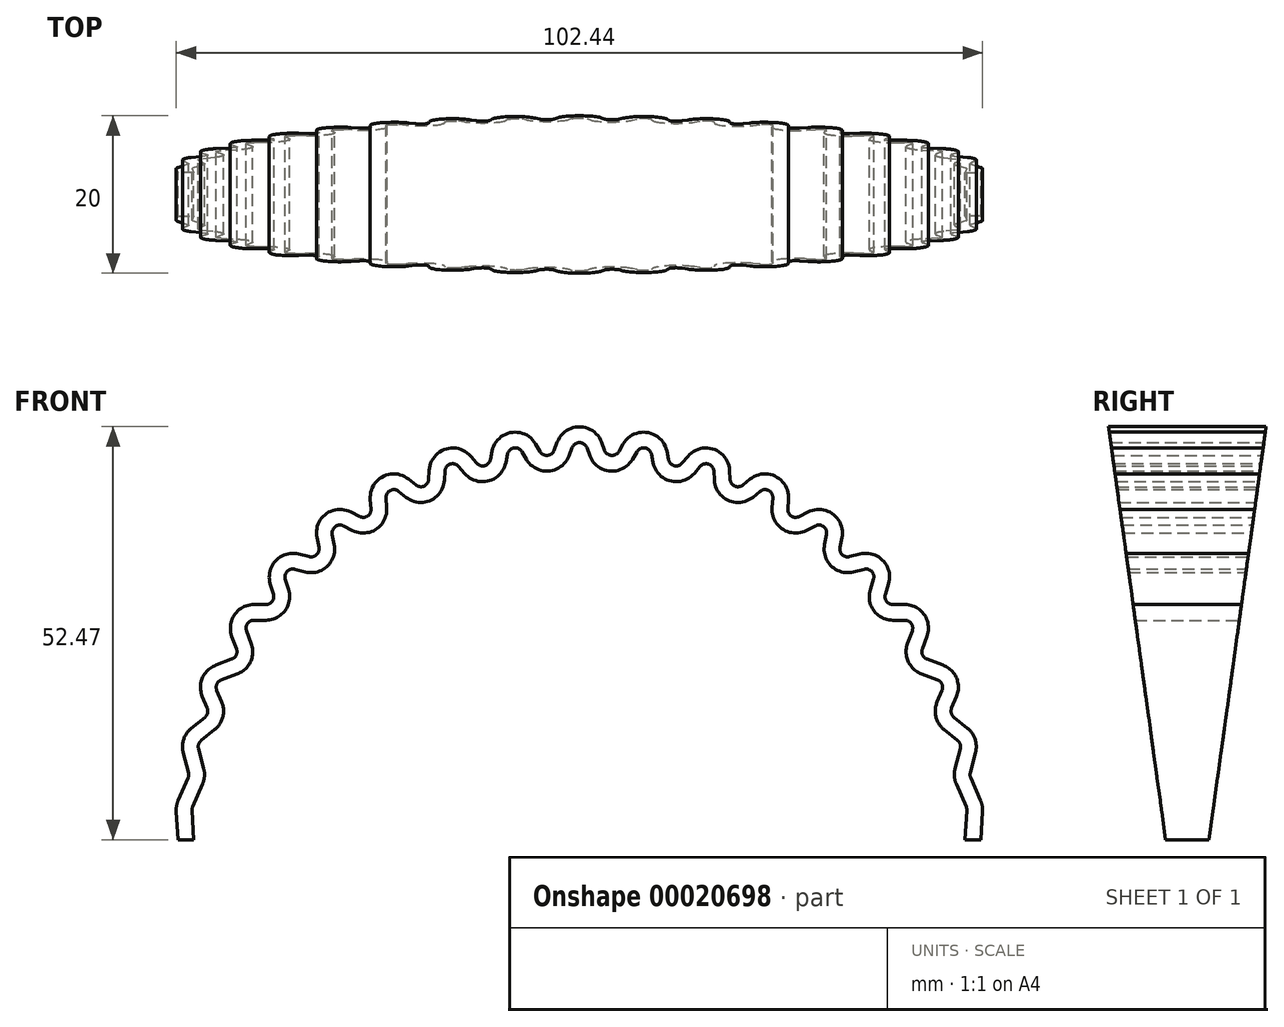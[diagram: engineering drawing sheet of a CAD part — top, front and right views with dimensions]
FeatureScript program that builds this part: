
annotation { "Feature Type Name" : "Feature", "Feature Type Description" : "" }
export const myFeature = defineFeature(function(context is Context, id is Id, definition is map)
    precondition{}
    {
        {
            var Q0;
            Q0=qCreatedBy(makeId("Front.planeOp"),FACE);
            var sketch = newSketch(context, id + "F0", { "sketchPlane" : qUnion([Q0])});
            skCircle(sketch, "E0", {"center": v(0, 0) * mm, "radius": 50 * mm});
            skCircle(sketch, "E1", {"center": v(0, 5) * mm, "radius": 50.25 * mm});
            skCircle(sketch, "E2", {"center": v(0, -5) * mm, "radius": 50.25 * mm});
            skLineSegment(sketch, "E3", {"start": v(0, 0) * mm, "end": v(-50, 0) * mm, "construction": true});
            skLineSegment(sketch, "E4.1.0", {"start": v(0, 0) * mm, "end": v(-49.83, 4.13) * mm, "construction": true});
            skLineSegment(sketch, "E4.2.0", {"start": v(0, 0) * mm, "end": v(-49.32, 8.23) * mm, "construction": true});
            skLineSegment(sketch, "E4.3.0", {"start": v(0, 0) * mm, "end": v(-48.47, 12.27) * mm, "construction": true});
            skLineSegment(sketch, "E4.4.0", {"start": v(0, 0) * mm, "end": v(-47.3, 16.23) * mm, "construction": true});
            skLineSegment(sketch, "E4.5.0", {"start": v(0, 0) * mm, "end": v(-45.79, 20.08) * mm, "construction": true});
            skLineSegment(sketch, "E4.6.0", {"start": v(0, 0) * mm, "end": v(-43.97, 23.8) * mm, "construction": true});
            skLineSegment(sketch, "E4.7.0", {"start": v(0, 0) * mm, "end": v(-41.86, 27.35) * mm, "construction": true});
            skLineSegment(sketch, "E4.anchor2", {"start": v(0, 0) * mm, "end": v(0, 50) * mm, "construction": true});
            skLineSegment(sketch, "E5.2.8.0", {"start": v(0, 0) * mm, "end": v(-39.46, 30.71) * mm, "construction": true});
            skLineSegment(sketch, "E5.2.9.0", {"start": v(0, 0) * mm, "end": v(-36.79, 33.86) * mm, "construction": true});
            skLineSegment(sketch, "E5.2.10.0", {"start": v(0, 0) * mm, "end": v(-33.86, 36.79) * mm, "construction": true});
            skLineSegment(sketch, "E5.2.11.0", {"start": v(0, 0) * mm, "end": v(-30.71, 39.46) * mm, "construction": true});
            skLineSegment(sketch, "E5.2.12.0", {"start": v(0, 0) * mm, "end": v(-27.35, 41.86) * mm, "construction": true});
            skLineSegment(sketch, "E6.2.13.0", {"start": v(0, 0) * mm, "end": v(-23.8, 43.97) * mm, "construction": true});
            skLineSegment(sketch, "E6.2.14.0", {"start": v(0, 0) * mm, "end": v(-20.08, 45.79) * mm, "construction": true});
            skLineSegment(sketch, "E6.2.15.0", {"start": v(0, 0) * mm, "end": v(-16.23, 47.3) * mm, "construction": true});
            skLineSegment(sketch, "E6.2.16.0", {"start": v(0, 0) * mm, "end": v(-12.27, 48.47) * mm, "construction": true});
            skLineSegment(sketch, "E6.2.17.0", {"start": v(0, 0) * mm, "end": v(-8.23, 49.32) * mm, "construction": true});
            skLineSegment(sketch, "E6.2.18.0", {"start": v(0, 0) * mm, "end": v(-4.13, 49.83) * mm, "construction": true});
            skLineSegment(sketch, "E7", {"start": v(-50, 0) * mm, "end": v(-50.24, 4.13) * mm});
            skLineSegment(sketch, "E8", {"start": v(-50.24, 4.13) * mm, "end": v(-48.51, 8.1) * mm});
            skLineSegment(sketch, "E9", {"start": v(-48.51, 8.1) * mm, "end": v(-49.67, 12.58) * mm});
            skLineSegment(sketch, "E10", {"start": v(-49.67, 12.58) * mm, "end": v(-45.78, 15.72) * mm});
            skLineSegment(sketch, "E11", {"start": v(-45.78, 15.72) * mm, "end": v(-47.79, 20.54) * mm});
            skLineSegment(sketch, "E12", {"start": v(-47.79, 20.54) * mm, "end": v(-41.93, 22.7) * mm});
            skLineSegment(sketch, "E13", {"start": v(-41.93, 22.7) * mm, "end": v(-44.21, 28.88) * mm});
            skLineSegment(sketch, "E14", {"start": v(-44.21, 28.88) * mm, "end": v(-37.1, 28.88) * mm});
            skLineSegment(sketch, "E15", {"start": v(-37.1, 28.88) * mm, "end": v(-39.36, 36.24) * mm});
            skLineSegment(sketch, "E16", {"start": v(-39.36, 36.24) * mm, "end": v(-31.46, 34.18) * mm});
            skLineSegment(sketch, "E17", {"start": v(-31.46, 34.18) * mm, "end": v(-33.23, 42.7) * mm});
            skLineSegment(sketch, "E18", {"start": v(-33.23, 42.7) * mm, "end": v(-25.15, 38.5) * mm});
            skLineSegment(sketch, "E19", {"start": v(-25.15, 38.5) * mm, "end": v(-25.98, 48.01) * mm});
            skLineSegment(sketch, "E20", {"start": v(-25.98, 48.01) * mm, "end": v(-18.33, 41.79) * mm});
            skLineSegment(sketch, "E21", {"start": v(-18.33, 41.79) * mm, "end": v(-17.84, 51.97) * mm});
            skLineSegment(sketch, "E22", {"start": v(-17.84, 51.97) * mm, "end": v(-11.14, 44) * mm});
            skLineSegment(sketch, "E23", {"start": v(-11.14, 44) * mm, "end": v(-9.08, 54.42) * mm});
            skLineSegment(sketch, "E24", {"start": v(-9.08, 54.42) * mm, "end": v(-3.74, 45.11) * mm});
            skLineSegment(sketch, "E25", {"start": v(-3.74, 45.11) * mm, "end": v(0, 55.25) * mm});
            skSolve(sketch);
        }
        {
            var Q0;
            Q0=qCreatedBy(makeId("Front.planeOp"),FACE);
            var sketch = newSketch(context, id + "F1", { "sketchPlane" : qUnion([Q0])});
            skLineSegment(sketch, "E26.0", {"start": v(-2.26, 49.13) * mm, "end": v(-1.88, 50.16) * mm});
            skLineSegment(sketch, "E26.1", {"start": v(-6.42, 49.79) * mm, "end": v(-5.87, 48.82) * mm});
            skLineSegment(sketch, "E26.2", {"start": v(-10.33, 48.1) * mm, "end": v(-10.12, 49.18) * mm});
            skLineSegment(sketch, "E26.3", {"start": v(-14.56, 48.06) * mm, "end": v(-13.83, 47.2) * mm});
            skLineSegment(sketch, "E26.4", {"start": v(-18.14, 45.74) * mm, "end": v(-18.09, 46.87) * mm});
            skLineSegment(sketch, "E26.5", {"start": v(-22.32, 45.03) * mm, "end": v(-21.4, 44.28) * mm});
            skLineSegment(sketch, "E26.6", {"start": v(-25.47, 42.13) * mm, "end": v(-25.57, 43.3) * mm});
            skLineSegment(sketch, "E26.7", {"start": v(-29.5, 40.75) * mm, "end": v(-28.38, 40.18) * mm});
            skLineSegment(sketch, "E26.8", {"start": v(-32.12, 37.33) * mm, "end": v(-32.38, 38.57) * mm});
            skLineSegment(sketch, "E26.9", {"start": v(-35.9, 35.33) * mm, "end": v(-34.58, 35) * mm});
            skLineSegment(sketch, "E26.10", {"start": v(-37.9, 31.47) * mm, "end": v(-38.31, 32.81) * mm});
            skLineSegment(sketch, "E26.11", {"start": v(-41.34, 28.88) * mm, "end": v(-39.81, 28.88) * mm});
            skLineSegment(sketch, "E26.12", {"start": v(-42.62, 24.57) * mm, "end": v(-43.22, 26.2) * mm});
            skLineSegment(sketch, "E26.13", {"start": v(-45.83, 21.26) * mm, "end": v(-43.8, 22) * mm});
            skLineSegment(sketch, "E26.14", {"start": v(-46.36, 17.1) * mm, "end": v(-46.99, 18.61) * mm});
            skLineSegment(sketch, "E26.15", {"start": v(-48.67, 13.39) * mm, "end": v(-46.95, 14.78) * mm});
            skLineSegment(sketch, "E26.16", {"start": v(-48.69, 8.76) * mm, "end": v(-49.35, 11.33) * mm});
            skLineSegment(sketch, "E26.17", {"start": v(-50.05, 4.57) * mm, "end": v(-48.79, 7.46) * mm});
            skLineSegment(sketch, "E26.18", {"start": v(-50, 0) * mm, "end": v(-50.21, 3.65) * mm});
            skPoint(sketch, "E27.visualSharp", {"position": v(-50.24, 4.13) * mm});
            skArc(sketch, "E27.filletArc", {"start": v(-50.05, 4.57) * mm, "mid": v(-50.19, 4.12) * mm, "end": v(-50.21, 3.65) * mm});
            skPoint(sketch, "E28.visualSharp", {"position": v(-48.51, 8.1) * mm});
            skArc(sketch, "E28.filletArc", {"start": v(-48.79, 7.46) * mm, "mid": v(-48.63, 8.1) * mm, "end": v(-48.69, 8.76) * mm});
            skPoint(sketch, "E29.visualSharp", {"position": v(-49.67, 12.58) * mm});
            skArc(sketch, "E29.filletArc", {"start": v(-48.67, 13.39) * mm, "mid": v(-49.31, 12.46) * mm, "end": v(-49.35, 11.33) * mm});
            skPoint(sketch, "E30.visualSharp", {"position": v(-45.78, 15.72) * mm});
            skArc(sketch, "E30.filletArc", {"start": v(-46.95, 14.78) * mm, "mid": v(-46.27, 15.84) * mm, "end": v(-46.36, 17.1) * mm});
            skPoint(sketch, "E31.visualSharp", {"position": v(-47.79, 20.54) * mm});
            skArc(sketch, "E31.filletArc", {"start": v(-45.83, 21.26) * mm, "mid": v(-46.97, 20.18) * mm, "end": v(-46.99, 18.61) * mm});
            skPoint(sketch, "E32.visualSharp", {"position": v(-41.93, 22.7) * mm});
            skArc(sketch, "E32.filletArc", {"start": v(-43.8, 22) * mm, "mid": v(-42.68, 23.04) * mm, "end": v(-42.62, 24.57) * mm});
            skPoint(sketch, "E33.visualSharp", {"position": v(-44.21, 28.88) * mm});
            skArc(sketch, "E33.filletArc", {"start": v(-41.34, 28.88) * mm, "mid": v(-42.98, 28.03) * mm, "end": v(-43.22, 26.2) * mm});
            skPoint(sketch, "E34.visualSharp", {"position": v(-37.1, 28.88) * mm});
            skArc(sketch, "E34.filletArc", {"start": v(-39.81, 28.88) * mm, "mid": v(-38.2, 29.7) * mm, "end": v(-37.9, 31.47) * mm});
            skPoint(sketch, "E35.visualSharp", {"position": v(-39.36, 36.24) * mm});
            skArc(sketch, "E35.filletArc", {"start": v(-35.9, 35.33) * mm, "mid": v(-37.84, 34.78) * mm, "end": v(-38.31, 32.81) * mm});
            skPoint(sketch, "E36.visualSharp", {"position": v(-31.46, 34.18) * mm});
            skArc(sketch, "E36.filletArc", {"start": v(-34.58, 35) * mm, "mid": v(-32.7, 35.48) * mm, "end": v(-32.12, 37.33) * mm});
            skPoint(sketch, "E37.visualSharp", {"position": v(-33.23, 42.7) * mm});
            skArc(sketch, "E37.filletArc", {"start": v(-29.5, 40.75) * mm, "mid": v(-31.62, 40.57) * mm, "end": v(-32.38, 38.57) * mm});
            skPoint(sketch, "E38.visualSharp", {"position": v(-25.15, 38.5) * mm});
            skArc(sketch, "E38.filletArc", {"start": v(-28.38, 40.18) * mm, "mid": v(-26.35, 40.29) * mm, "end": v(-25.47, 42.13) * mm});
            skPoint(sketch, "E39.visualSharp", {"position": v(-25.98, 48.01) * mm});
            skArc(sketch, "E39.filletArc", {"start": v(-22.32, 45.03) * mm, "mid": v(-24.52, 45.25) * mm, "end": v(-25.57, 43.3) * mm});
            skPoint(sketch, "E40.visualSharp", {"position": v(-18.33, 41.79) * mm});
            skArc(sketch, "E40.filletArc", {"start": v(-21.4, 44.28) * mm, "mid": v(-19.32, 44.01) * mm, "end": v(-18.14, 45.74) * mm});
            skPoint(sketch, "E41.visualSharp", {"position": v(-17.84, 51.97) * mm});
            skArc(sketch, "E41.filletArc", {"start": v(-14.56, 48.06) * mm, "mid": v(-16.73, 48.67) * mm, "end": v(-18.09, 46.87) * mm});
            skPoint(sketch, "E42.visualSharp", {"position": v(-11.14, 44) * mm});
            skArc(sketch, "E42.filletArc", {"start": v(-13.83, 47.2) * mm, "mid": v(-11.8, 46.54) * mm, "end": v(-10.33, 48.1) * mm});
            skPoint(sketch, "E43.visualSharp", {"position": v(-9.08, 54.42) * mm});
            skArc(sketch, "E43.filletArc", {"start": v(-6.42, 49.79) * mm, "mid": v(-8.48, 50.76) * mm, "end": v(-10.12, 49.18) * mm});
            skPoint(sketch, "E44.visualSharp", {"position": v(-3.74, 45.11) * mm});
            skArc(sketch, "E44.filletArc", {"start": v(-5.87, 48.82) * mm, "mid": v(-3.97, 47.83) * mm, "end": v(-2.26, 49.13) * mm});
            skLineSegment(sketch, "E45", {"start": v(0, 0) * mm, "end": v(0, 51.47) * mm, "construction": true});
            skLineSegment(sketch, "E46.MirrorCS", {"start": v(2.26, 49.13) * mm, "end": v(1.88, 50.16) * mm, "construction": true});
            skPoint(sketch, "E47.visualSharp", {"position": v(0, 55.25) * mm});
            skArc(sketch, "E47.filletArc", {"start": v(0, 51.47) * mm, "mid": v(-1.14, 51.1) * mm, "end": v(-1.88, 50.16) * mm});
            skArc(sketch, "E48.0", {"start": v(0, 50.47) * mm, "mid": v(-0.57, 50.29) * mm, "end": v(-0.94, 49.81) * mm});
            skLineSegment(sketch, "E48.1", {"start": v(-1.32, 48.78) * mm, "end": v(-0.94, 49.81) * mm});
            skArc(sketch, "E48.2", {"start": v(-6.74, 48.33) * mm, "mid": v(-3.88, 46.83) * mm, "end": v(-1.32, 48.78) * mm});
            skLineSegment(sketch, "E48.3", {"start": v(-7.29, 49.29) * mm, "end": v(-6.74, 48.33) * mm});
            skArc(sketch, "E48.4", {"start": v(-7.29, 49.29) * mm, "mid": v(-8.32, 49.78) * mm, "end": v(-9.14, 48.98) * mm});
            skLineSegment(sketch, "E48.5", {"start": v(-9.35, 47.9) * mm, "end": v(-9.14, 48.98) * mm});
            skArc(sketch, "E48.6", {"start": v(-14.6, 46.55) * mm, "mid": v(-11.55, 45.57) * mm, "end": v(-9.35, 47.9) * mm});
            skLineSegment(sketch, "E48.7", {"start": v(-15.32, 47.42) * mm, "end": v(-14.6, 46.55) * mm});
            skArc(sketch, "E48.8", {"start": v(-15.32, 47.42) * mm, "mid": v(-16.4, 47.73) * mm, "end": v(-17.09, 46.83) * mm});
            skLineSegment(sketch, "E48.9", {"start": v(-17.14, 45.7) * mm, "end": v(-17.09, 46.83) * mm});
            skArc(sketch, "E48.10", {"start": v(-22.03, 43.5) * mm, "mid": v(-18.91, 43.1) * mm, "end": v(-17.14, 45.7) * mm});
            skLineSegment(sketch, "E48.11", {"start": v(-22.95, 44.25) * mm, "end": v(-22.03, 43.5) * mm});
            skArc(sketch, "E48.12", {"start": v(-22.95, 44.25) * mm, "mid": v(-24.05, 44.36) * mm, "end": v(-24.58, 43.4) * mm});
            skLineSegment(sketch, "E48.13", {"start": v(-24.47, 42.21) * mm, "end": v(-24.58, 43.4) * mm});
            skArc(sketch, "E48.14", {"start": v(-28.84, 39.29) * mm, "mid": v(-25.8, 39.46) * mm, "end": v(-24.47, 42.21) * mm});
            skLineSegment(sketch, "E48.15", {"start": v(-29.96, 39.87) * mm, "end": v(-28.84, 39.29) * mm});
            skLineSegment(sketch, "E48.16", {"start": v(-49, 0) * mm, "end": v(-49.22, 3.7) * mm});
            skArc(sketch, "E48.17", {"start": v(-49.13, 4.17) * mm, "mid": v(-49.2, 3.94) * mm, "end": v(-49.22, 3.7) * mm});
            skLineSegment(sketch, "E48.18", {"start": v(-49.13, 4.17) * mm, "end": v(-47.87, 7.06) * mm});
            skArc(sketch, "E48.19", {"start": v(-47.87, 7.06) * mm, "mid": v(-47.63, 8.03) * mm, "end": v(-47.72, 9.01) * mm});
            skLineSegment(sketch, "E48.20", {"start": v(-47.72, 9.01) * mm, "end": v(-48.38, 11.58) * mm});
            skArc(sketch, "E48.21", {"start": v(-48.04, 12.61) * mm, "mid": v(-48.36, 12.15) * mm, "end": v(-48.38, 11.58) * mm});
            skLineSegment(sketch, "E48.22", {"start": v(-48.04, 12.61) * mm, "end": v(-46.32, 14) * mm});
            skArc(sketch, "E48.23", {"start": v(-46.32, 14) * mm, "mid": v(-45.3, 15.6) * mm, "end": v(-45.43, 17.49) * mm});
            skLineSegment(sketch, "E48.24", {"start": v(-45.43, 17.49) * mm, "end": v(-46.06, 19) * mm});
            skArc(sketch, "E48.25", {"start": v(-45.48, 20.32) * mm, "mid": v(-46.06, 19.78) * mm, "end": v(-46.06, 19) * mm});
            skLineSegment(sketch, "E48.26", {"start": v(-45.48, 20.32) * mm, "end": v(-43.46, 21.06) * mm});
            skArc(sketch, "E48.27", {"start": v(-43.46, 21.06) * mm, "mid": v(-41.77, 22.62) * mm, "end": v(-41.68, 24.91) * mm});
            skLineSegment(sketch, "E48.28", {"start": v(-41.68, 24.91) * mm, "end": v(-42.28, 26.54) * mm});
            skArc(sketch, "E48.29", {"start": v(-41.34, 27.88) * mm, "mid": v(-42.16, 27.46) * mm, "end": v(-42.28, 26.54) * mm});
            skLineSegment(sketch, "E48.30", {"start": v(-41.34, 27.88) * mm, "end": v(-39.81, 27.88) * mm});
            skArc(sketch, "E48.31", {"start": v(-39.81, 27.88) * mm, "mid": v(-37.4, 29.1) * mm, "end": v(-36.94, 31.76) * mm});
            skLineSegment(sketch, "E48.32", {"start": v(-36.94, 31.76) * mm, "end": v(-37.36, 33.1) * mm});
            skArc(sketch, "E48.33", {"start": v(-36.15, 34.36) * mm, "mid": v(-37.12, 34.09) * mm, "end": v(-37.36, 33.1) * mm});
            skLineSegment(sketch, "E48.34", {"start": v(-36.15, 34.36) * mm, "end": v(-34.83, 34.02) * mm});
            skArc(sketch, "E48.35", {"start": v(-34.83, 34.02) * mm, "mid": v(-32, 34.75) * mm, "end": v(-31.14, 37.53) * mm});
            skLineSegment(sketch, "E48.36", {"start": v(-31.14, 37.53) * mm, "end": v(-31.4, 38.78) * mm});
            skArc(sketch, "E48.37", {"start": v(-29.96, 39.87) * mm, "mid": v(-31.02, 39.78) * mm, "end": v(-31.4, 38.78) * mm});
            skArc(sketch, "E49.0", {"start": v(0, 52.47) * mm, "mid": v(-1.72, 51.93) * mm, "end": v(-2.81, 50.5) * mm});
            skLineSegment(sketch, "E49.1", {"start": v(-3.2, 49.47) * mm, "end": v(-2.81, 50.5) * mm});
            skArc(sketch, "E49.2", {"start": v(-5, 49.32) * mm, "mid": v(-4.05, 48.82) * mm, "end": v(-3.2, 49.47) * mm});
            skLineSegment(sketch, "E49.3", {"start": v(-5.55, 50.28) * mm, "end": v(-5, 49.32) * mm});
            skArc(sketch, "E49.4", {"start": v(-5.55, 50.28) * mm, "mid": v(-8.64, 51.75) * mm, "end": v(-11.1, 49.37) * mm});
            skLineSegment(sketch, "E49.5", {"start": v(-11.31, 48.29) * mm, "end": v(-11.1, 49.37) * mm});
            skArc(sketch, "E49.6", {"start": v(-13.06, 47.84) * mm, "mid": v(-12.05, 47.51) * mm, "end": v(-11.31, 48.29) * mm});
            skLineSegment(sketch, "E49.7", {"start": v(-13.8, 48.7) * mm, "end": v(-13.06, 47.84) * mm});
            skArc(sketch, "E49.8", {"start": v(-13.8, 48.7) * mm, "mid": v(-17.05, 49.62) * mm, "end": v(-19.09, 46.92) * mm});
            skLineSegment(sketch, "E49.9", {"start": v(-19.14, 45.79) * mm, "end": v(-19.09, 46.92) * mm});
            skArc(sketch, "E49.10", {"start": v(-20.77, 45.06) * mm, "mid": v(-19.73, 44.92) * mm, "end": v(-19.14, 45.79) * mm});
            skLineSegment(sketch, "E49.11", {"start": v(-21.69, 45.8) * mm, "end": v(-20.77, 45.06) * mm});
            skArc(sketch, "E49.12", {"start": v(-21.69, 45.8) * mm, "mid": v(-24.98, 46.13) * mm, "end": v(-26.57, 43.22) * mm});
            skLineSegment(sketch, "E49.13", {"start": v(-26.47, 42.04) * mm, "end": v(-26.57, 43.22) * mm});
            skArc(sketch, "E49.14", {"start": v(-27.92, 41.06) * mm, "mid": v(-26.9, 41.12) * mm, "end": v(-26.47, 42.04) * mm});
            skLineSegment(sketch, "E49.15", {"start": v(-29.03, 41.64) * mm, "end": v(-27.92, 41.06) * mm});
            skLineSegment(sketch, "E49.16", {"start": v(-51, 0) * mm, "end": v(-51.21, 3.6) * mm});
            skArc(sketch, "E49.17", {"start": v(-50.97, 4.97) * mm, "mid": v(-51.17, 4.3) * mm, "end": v(-51.21, 3.6) * mm});
            skLineSegment(sketch, "E49.18", {"start": v(-50.97, 4.97) * mm, "end": v(-49.7, 7.86) * mm});
            skArc(sketch, "E49.19", {"start": v(-49.7, 7.86) * mm, "mid": v(-49.63, 8.18) * mm, "end": v(-49.65, 8.51) * mm});
            skLineSegment(sketch, "E49.20", {"start": v(-49.65, 8.51) * mm, "end": v(-50.32, 11.08) * mm});
            skArc(sketch, "E49.21", {"start": v(-49.3, 14.17) * mm, "mid": v(-50.26, 12.77) * mm, "end": v(-50.32, 11.08) * mm});
            skLineSegment(sketch, "E49.22", {"start": v(-49.3, 14.17) * mm, "end": v(-47.58, 15.55) * mm});
            skArc(sketch, "E49.23", {"start": v(-47.58, 15.55) * mm, "mid": v(-47.23, 16.09) * mm, "end": v(-47.28, 16.72) * mm});
            skLineSegment(sketch, "E49.24", {"start": v(-47.28, 16.72) * mm, "end": v(-47.9, 18.23) * mm});
            skArc(sketch, "E49.25", {"start": v(-46.18, 22.2) * mm, "mid": v(-47.89, 20.58) * mm, "end": v(-47.9, 18.23) * mm});
            skLineSegment(sketch, "E49.26", {"start": v(-46.18, 22.2) * mm, "end": v(-44.15, 22.94) * mm});
            skArc(sketch, "E49.27", {"start": v(-44.15, 22.94) * mm, "mid": v(-43.6, 23.46) * mm, "end": v(-43.56, 24.22) * mm});
            skLineSegment(sketch, "E49.28", {"start": v(-43.56, 24.22) * mm, "end": v(-44.16, 25.85) * mm});
            skArc(sketch, "E49.29", {"start": v(-41.34, 29.88) * mm, "mid": v(-43.8, 28.6) * mm, "end": v(-44.16, 25.85) * mm});
            skLineSegment(sketch, "E49.30", {"start": v(-41.34, 29.88) * mm, "end": v(-39.81, 29.88) * mm});
            skArc(sketch, "E49.31", {"start": v(-39.81, 29.88) * mm, "mid": v(-39, 30.29) * mm, "end": v(-38.86, 31.18) * mm});
            skLineSegment(sketch, "E49.32", {"start": v(-38.86, 31.18) * mm, "end": v(-39.27, 32.52) * mm});
            skArc(sketch, "E49.33", {"start": v(-35.64, 36.3) * mm, "mid": v(-38.57, 35.47) * mm, "end": v(-39.27, 32.52) * mm});
            skLineSegment(sketch, "E49.34", {"start": v(-35.64, 36.3) * mm, "end": v(-34.33, 35.96) * mm});
            skArc(sketch, "E49.35", {"start": v(-34.33, 35.96) * mm, "mid": v(-33.39, 36.2) * mm, "end": v(-33.1, 37.13) * mm});
            skLineSegment(sketch, "E49.36", {"start": v(-33.1, 37.13) * mm, "end": v(-33.35, 38.37) * mm});
            skArc(sketch, "E49.37", {"start": v(-29.03, 41.64) * mm, "mid": v(-32.23, 41.37) * mm, "end": v(-33.35, 38.37) * mm});
            skLineSegment(sketch, "E50", {"start": v(-51, 0) * mm, "end": v(-49, 0) * mm});
            skLineSegment(sketch, "E51", {"start": v(0, 50.47) * mm, "end": v(0, 52.47) * mm});
            skSolve(sketch);
        }
        {
            var Q0;
            Q0 = qSketchRegion(id + "F1", true);
            extrude(context, id + "F2", {"entities" : qUnion([Q0]), "endBound" : BoundingType.SYMMETRIC, "depth" : 20 * mm});
        }
        {
            var Q0;
            Q0=qCreatedBy(makeId("Right.planeOp"),FACE);
            var sketch = newSketch(context, id + "F3", { "sketchPlane" : qUnion([Q0])});
            skLineSegment(sketch, "E52", {"start": v(10, 52.47) * mm, "end": v(-10, 52.47) * mm});
            skLineSegment(sketch, "E53", {"start": v(-10, 52.47) * mm, "end": v(0, -20) * mm});
            skLineSegment(sketch, "E54", {"start": v(0, -20) * mm, "end": v(10, 52.47) * mm});
            skSolve(sketch);
        }
        {
            var Q0;
            Q0 = qSketchRegion(id + "F3", true);
            extrude(context, id + "F4", {"entities" : qUnion([Q0]), "operationType" : NewBodyOperationType.INTERSECT, "endBound" : BoundingType.THROUGH_ALL, "oppositeDirection" : true, "depth" : 25 * mm});
        }
        {
            var Q0;
            Q0=makeQuery(id+"F2.opExtrude","SWEPT_BODY",BODY,{"disambiguationData":[OSD([sQuery(id+"F1.wireOp",EDGE,"E48.0"),sQuery(id+"F1.wireOp",EDGE,"E48.1"),sQuery(id+"F1.wireOp",EDGE,"E48.2"),sQuery(id+"F1.wireOp",EDGE,"E48.3"),sQuery(id+"F1.wireOp",EDGE,"E48.4"),sQuery(id+"F1.wireOp",EDGE,"E48.5"),sQuery(id+"F1.wireOp",EDGE,"E48.6"),sQuery(id+"F1.wireOp",EDGE,"E48.7"),sQuery(id+"F1.wireOp",EDGE,"E48.8"),sQuery(id+"F1.wireOp",EDGE,"E48.9"),sQuery(id+"F1.wireOp",EDGE,"E48.10"),sQuery(id+"F1.wireOp",EDGE,"E48.11"),sQuery(id+"F1.wireOp",EDGE,"E48.12"),sQuery(id+"F1.wireOp",EDGE,"E48.13"),sQuery(id+"F1.wireOp",EDGE,"E48.14"),sQuery(id+"F1.wireOp",EDGE,"E48.15"),sQuery(id+"F1.wireOp",EDGE,"E48.16"),sQuery(id+"F1.wireOp",EDGE,"E48.17"),sQuery(id+"F1.wireOp",EDGE,"E48.18"),sQuery(id+"F1.wireOp",EDGE,"E48.19"),sQuery(id+"F1.wireOp",EDGE,"E48.20"),sQuery(id+"F1.wireOp",EDGE,"E48.21"),sQuery(id+"F1.wireOp",EDGE,"E48.22"),sQuery(id+"F1.wireOp",EDGE,"E48.23"),sQuery(id+"F1.wireOp",EDGE,"E48.24"),sQuery(id+"F1.wireOp",EDGE,"E48.25"),sQuery(id+"F1.wireOp",EDGE,"E48.26"),sQuery(id+"F1.wireOp",EDGE,"E48.27"),sQuery(id+"F1.wireOp",EDGE,"E48.28"),sQuery(id+"F1.wireOp",EDGE,"E48.29"),sQuery(id+"F1.wireOp",EDGE,"E48.30"),sQuery(id+"F1.wireOp",EDGE,"E48.31"),sQuery(id+"F1.wireOp",EDGE,"E48.32"),sQuery(id+"F1.wireOp",EDGE,"E48.33"),sQuery(id+"F1.wireOp",EDGE,"E48.34"),sQuery(id+"F1.wireOp",EDGE,"E48.35"),sQuery(id+"F1.wireOp",EDGE,"E48.36"),sQuery(id+"F1.wireOp",EDGE,"E48.37"),sQuery(id+"F1.wireOp",EDGE,"E49.0"),sQuery(id+"F1.wireOp",EDGE,"E49.1"),sQuery(id+"F1.wireOp",EDGE,"E49.2"),sQuery(id+"F1.wireOp",EDGE,"E49.3"),sQuery(id+"F1.wireOp",EDGE,"E49.4"),sQuery(id+"F1.wireOp",EDGE,"E49.5"),sQuery(id+"F1.wireOp",EDGE,"E49.6"),sQuery(id+"F1.wireOp",EDGE,"E49.7"),sQuery(id+"F1.wireOp",EDGE,"E49.8"),sQuery(id+"F1.wireOp",EDGE,"E49.9"),sQuery(id+"F1.wireOp",EDGE,"E49.10"),sQuery(id+"F1.wireOp",EDGE,"E49.11"),sQuery(id+"F1.wireOp",EDGE,"E49.12"),sQuery(id+"F1.wireOp",EDGE,"E49.13"),sQuery(id+"F1.wireOp",EDGE,"E49.14"),sQuery(id+"F1.wireOp",EDGE,"E49.15"),sQuery(id+"F1.wireOp",EDGE,"E49.16"),sQuery(id+"F1.wireOp",EDGE,"E49.17"),sQuery(id+"F1.wireOp",EDGE,"E49.18"),sQuery(id+"F1.wireOp",EDGE,"E49.19"),sQuery(id+"F1.wireOp",EDGE,"E49.20"),sQuery(id+"F1.wireOp",EDGE,"E49.21"),sQuery(id+"F1.wireOp",EDGE,"E49.22"),sQuery(id+"F1.wireOp",EDGE,"E49.23"),sQuery(id+"F1.wireOp",EDGE,"E49.24"),sQuery(id+"F1.wireOp",EDGE,"E49.25"),sQuery(id+"F1.wireOp",EDGE,"E49.26"),sQuery(id+"F1.wireOp",EDGE,"E49.27"),sQuery(id+"F1.wireOp",EDGE,"E49.28"),sQuery(id+"F1.wireOp",EDGE,"E49.29"),sQuery(id+"F1.wireOp",EDGE,"E49.30"),sQuery(id+"F1.wireOp",EDGE,"E49.31"),sQuery(id+"F1.wireOp",EDGE,"E49.32"),sQuery(id+"F1.wireOp",EDGE,"E49.33"),sQuery(id+"F1.wireOp",EDGE,"E49.34"),sQuery(id+"F1.wireOp",EDGE,"E49.35"),sQuery(id+"F1.wireOp",EDGE,"E49.36"),sQuery(id+"F1.wireOp",EDGE,"E49.37"),sQuery(id+"F1.wireOp",EDGE,"E50"),sQuery(id+"F1.wireOp",EDGE,"E51")])]});
            var Q1;
            Q1=qCreatedBy(makeId("Right.planeOp"),FACE);
            mirror(context, id + "F5", {"operationType" : NewBodyOperationType.ADD, "entities" : qUnion([Q0]), "mirrorPlane" : qUnion([Q1])});
        }
    });
